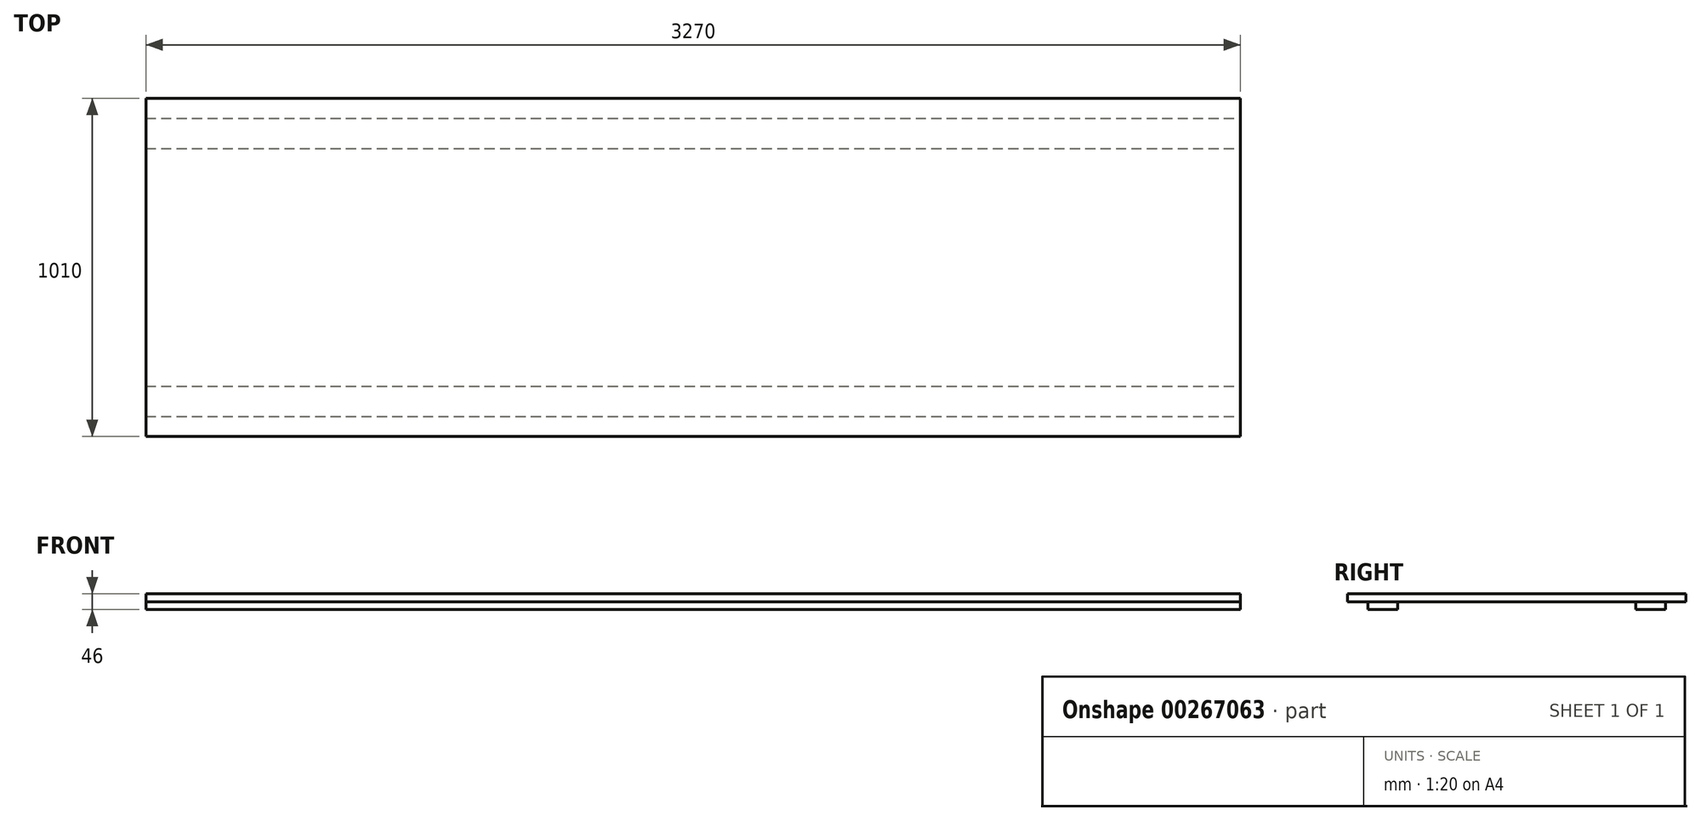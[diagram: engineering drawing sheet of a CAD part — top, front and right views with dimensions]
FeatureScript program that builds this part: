
annotation { "Feature Type Name" : "Feature", "Feature Type Description" : "" }
export const myFeature = defineFeature(function(context is Context, id is Id, definition is map)
    precondition{}
    {
        {
            var Q0;
            Q0=qCreatedBy(makeId("Top.planeOp"),FACE);
            var sketch = newSketch(context, id + "F0", { "sketchPlane" : qUnion([Q0])});
            skLineSegment(sketch, "E0.bottom", {"start": v(0, 0) * mm, "end": v(3270, 0) * mm});
            skLineSegment(sketch, "E0.top", {"start": v(0, 1010) * mm, "end": v(3270, 1010) * mm});
            skLineSegment(sketch, "E0.left", {"start": v(0, 0) * mm, "end": v(0, 1010) * mm});
            skLineSegment(sketch, "E0.right", {"start": v(3270, 0) * mm, "end": v(3270, 1010) * mm});
            skSolve(sketch);
        }
        {
            var Q0;
            Q0=makeQuery(id+"F0.imprint","IMPRINT",FACE,{"disambiguationData":[TD([[makeQuery(id+"F0.imprint","IMPRINT",EDGE,{"derivedFrom":sQuery(id+"F0.wireOp",EDGE,"E0.bottom")}),1.0]])]});
            extrude(context, id + "F1", {"entities" : qUnion([Q0]), "depth" : 23 * mm});
        }
        {
            var Q0;
            Q0=makeQuery(id+"F1.opExtrude","CAP_FACE",FACE,{"disambiguationData":[OSD([sQuery(id+"F0.wireOp",EDGE,"E0.bottom"),sQuery(id+"F0.wireOp",EDGE,"E0.top"),sQuery(id+"F0.wireOp",EDGE,"E0.left"),sQuery(id+"F0.wireOp",EDGE,"E0.right")])],"isStart":true});
            var sketch = newSketch(context, id + "F2", { "sketchPlane" : qUnion([Q0])});
            skLineSegment(sketch, "E1.0", {"start": v(0, 0) * mm, "end": v(0, -1010) * mm});
            skLineSegment(sketch, "E2.0", {"start": v(3270, 0) * mm, "end": v(3270, -1010) * mm});
            skLineSegment(sketch, "E3", {"start": v(0, -60) * mm, "end": v(3270, -60) * mm});
            skLineSegment(sketch, "E4", {"start": v(0, -150) * mm, "end": v(3270, -150) * mm});
            skLineSegment(sketch, "E5", {"start": v(0, -860) * mm, "end": v(3270, -860) * mm});
            skLineSegment(sketch, "E6", {"start": v(0, -950) * mm, "end": v(3270, -950) * mm});
            skLineSegment(sketch, "E7", {"start": v(0, -505) * mm, "end": v(3270, -505) * mm, "construction": true});
            skSolve(sketch);
        }
        {
            var Q0;
            {var subQ0=sQuery(id+"F2.wireOp",EDGE,"E3");Q0=makeQuery(id+"F2.imprint","IMPRINT",FACE,{"disambiguationData":[TD([[makeQuery(id+"F2.imprint","IMPRINT",EDGE,{"derivedFrom":subQ0}),-1.0]])]});}
            var Q1;
            {var subQ0=sQuery(id+"F2.wireOp",EDGE,"E5");Q1=makeQuery(id+"F2.imprint","IMPRINT",FACE,{"disambiguationData":[TD([[makeQuery(id+"F2.imprint","IMPRINT",EDGE,{"derivedFrom":subQ0}),-1.0]])]});}
            extrude(context, id + "F3", {"entities" : qUnion([Q0, Q1]), "depth" : 23 * mm});
        }
    });
